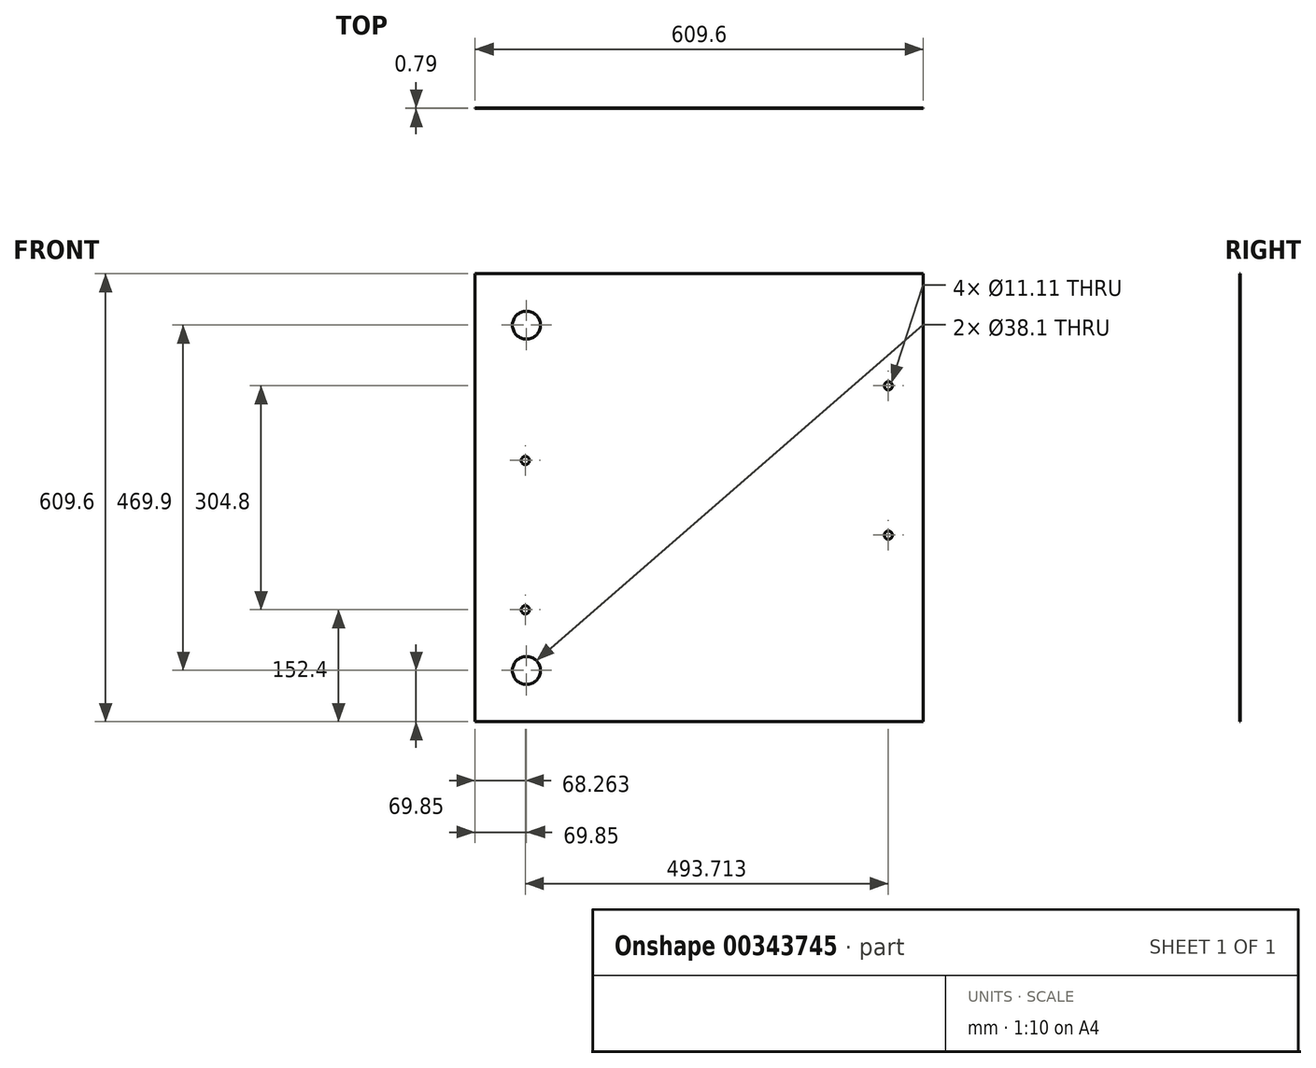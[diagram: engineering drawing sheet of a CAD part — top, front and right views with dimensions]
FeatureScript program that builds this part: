
annotation { "Feature Type Name" : "Feature", "Feature Type Description" : "" }
export const myFeature = defineFeature(function(context is Context, id is Id, definition is map)
    precondition{}
    {
        {
            var Q0;
            Q0=qCreatedBy(makeId("Front.planeOp"),FACE);
            var sketch = newSketch(context, id + "F0", { "sketchPlane" : qUnion([Q0])});
            skLineSegment(sketch, "E0.bottom", {"start": v(0, 0) * mm, "end": v(609.6, 0) * mm});
            skLineSegment(sketch, "E0.top", {"start": v(0, 609.6) * mm, "end": v(609.6, 609.6) * mm});
            skLineSegment(sketch, "E0.left", {"start": v(0, 0) * mm, "end": v(0, 609.6) * mm});
            skLineSegment(sketch, "E0.right", {"start": v(609.6, 0) * mm, "end": v(609.6, 609.6) * mm});
            skSolve(sketch);
        }
        {
            var Q0;
            Q0=makeQuery(id+"F0.imprint","IMPRINT",FACE,{"disambiguationData":[TD([[makeQuery(id+"F0.imprint","IMPRINT",EDGE,{"derivedFrom":sQuery(id+"F0.wireOp",EDGE,"E0.bottom")}),1.0]])]});
            extrude(context, id + "F1", {"entities" : qUnion([Q0]), "depth" : 0.8 * mm});
        }
        {
            var Q0;
            Q0=makeQuery(id+"F1.opExtrude","CAP_FACE",FACE,{"disambiguationData":[OSD([sQuery(id+"F0.wireOp",EDGE,"E0.bottom"),sQuery(id+"F0.wireOp",EDGE,"E0.top"),sQuery(id+"F0.wireOp",EDGE,"E0.left"),sQuery(id+"F0.wireOp",EDGE,"E0.right")])],"isStart":false});
            var sketch = newSketch(context, id + "F2", { "sketchPlane" : qUnion([Q0])});
            skCircle(sketch, "E1", {"center": v(68.26, 152.4) * mm, "radius": 5.56 * mm});
            skCircle(sketch, "E2", {"center": v(68.26, 355.6) * mm, "radius": 5.56 * mm});
            skCircle(sketch, "E3", {"center": v(561.98, 457.2) * mm, "radius": 5.56 * mm});
            skCircle(sketch, "E4", {"center": v(561.98, 254) * mm, "radius": 5.56 * mm});
            skSolve(sketch);
        }
        {
            var Q0;
            Q0=makeQuery(id+"F2.imprint","IMPRINT",FACE,{"disambiguationData":[TD([[makeQuery(id+"F2.imprint","IMPRINT",EDGE,{"derivedFrom":sQuery(id+"F2.wireOp",EDGE,"E2")}),1.0]])]});
            var Q1;
            Q1=makeQuery(id+"F2.imprint","IMPRINT",FACE,{"disambiguationData":[TD([[makeQuery(id+"F2.imprint","IMPRINT",EDGE,{"derivedFrom":sQuery(id+"F2.wireOp",EDGE,"E1")}),1.0]])]});
            var Q2;
            Q2=makeQuery(id+"F2.imprint","IMPRINT",FACE,{"disambiguationData":[TD([[makeQuery(id+"F2.imprint","IMPRINT",EDGE,{"derivedFrom":sQuery(id+"F2.wireOp",EDGE,"E4")}),1.0]])]});
            var Q3;
            Q3=makeQuery(id+"F2.imprint","IMPRINT",FACE,{"disambiguationData":[TD([[makeQuery(id+"F2.imprint","IMPRINT",EDGE,{"derivedFrom":sQuery(id+"F2.wireOp",EDGE,"E3")}),1.0]])]});
            extrude(context, id + "F3", {"entities" : qUnion([Q0, Q1, Q2, Q3]), "operationType" : NewBodyOperationType.REMOVE, "oppositeDirection" : true, "depth" : 25.4 * mm});
        }
        {
            var Q0;
            Q0=makeQuery(id+"F1.opExtrude","CAP_FACE",FACE,{"disambiguationData":[OSD([sQuery(id+"F0.wireOp",EDGE,"E0.bottom"),sQuery(id+"F0.wireOp",EDGE,"E0.top"),sQuery(id+"F0.wireOp",EDGE,"E0.left"),sQuery(id+"F0.wireOp",EDGE,"E0.right")])],"isStart":false});
            var sketch = newSketch(context, id + "F4", { "sketchPlane" : qUnion([Q0])});
            skCircle(sketch, "E5", {"center": v(69.85, 69.85) * mm, "radius": 19.05 * mm});
            skCircle(sketch, "E6", {"center": v(69.85, 539.75) * mm, "radius": 19.05 * mm});
            skSolve(sketch);
        }
        {
            var Q0;
            Q0=makeQuery(id+"F4.imprint","IMPRINT",FACE,{"disambiguationData":[TD([[makeQuery(id+"F4.imprint","IMPRINT",EDGE,{"derivedFrom":sQuery(id+"F4.wireOp",EDGE,"E5")}),1.0]])]});
            var Q1;
            Q1=makeQuery(id+"F4.imprint","IMPRINT",FACE,{"disambiguationData":[TD([[makeQuery(id+"F4.imprint","IMPRINT",EDGE,{"derivedFrom":sQuery(id+"F4.wireOp",EDGE,"eCU4ZGUX-AVk7-aPuw-nbNw-Pcqziy9d8Htn")}),1.0]])]});
            var Q2;
            Q2=makeQuery(id+"F4.imprint","IMPRINT",FACE,{"disambiguationData":[TD([[makeQuery(id+"F4.imprint","IMPRINT",EDGE,{"derivedFrom":sQuery(id+"F4.wireOp",EDGE,"E6")}),1.0]])]});
            extrude(context, id + "F5", {"entities" : qUnion([Q0, Q1, Q2]), "operationType" : NewBodyOperationType.REMOVE, "oppositeDirection" : true, "depth" : 25.4 * mm});
        }
    });
